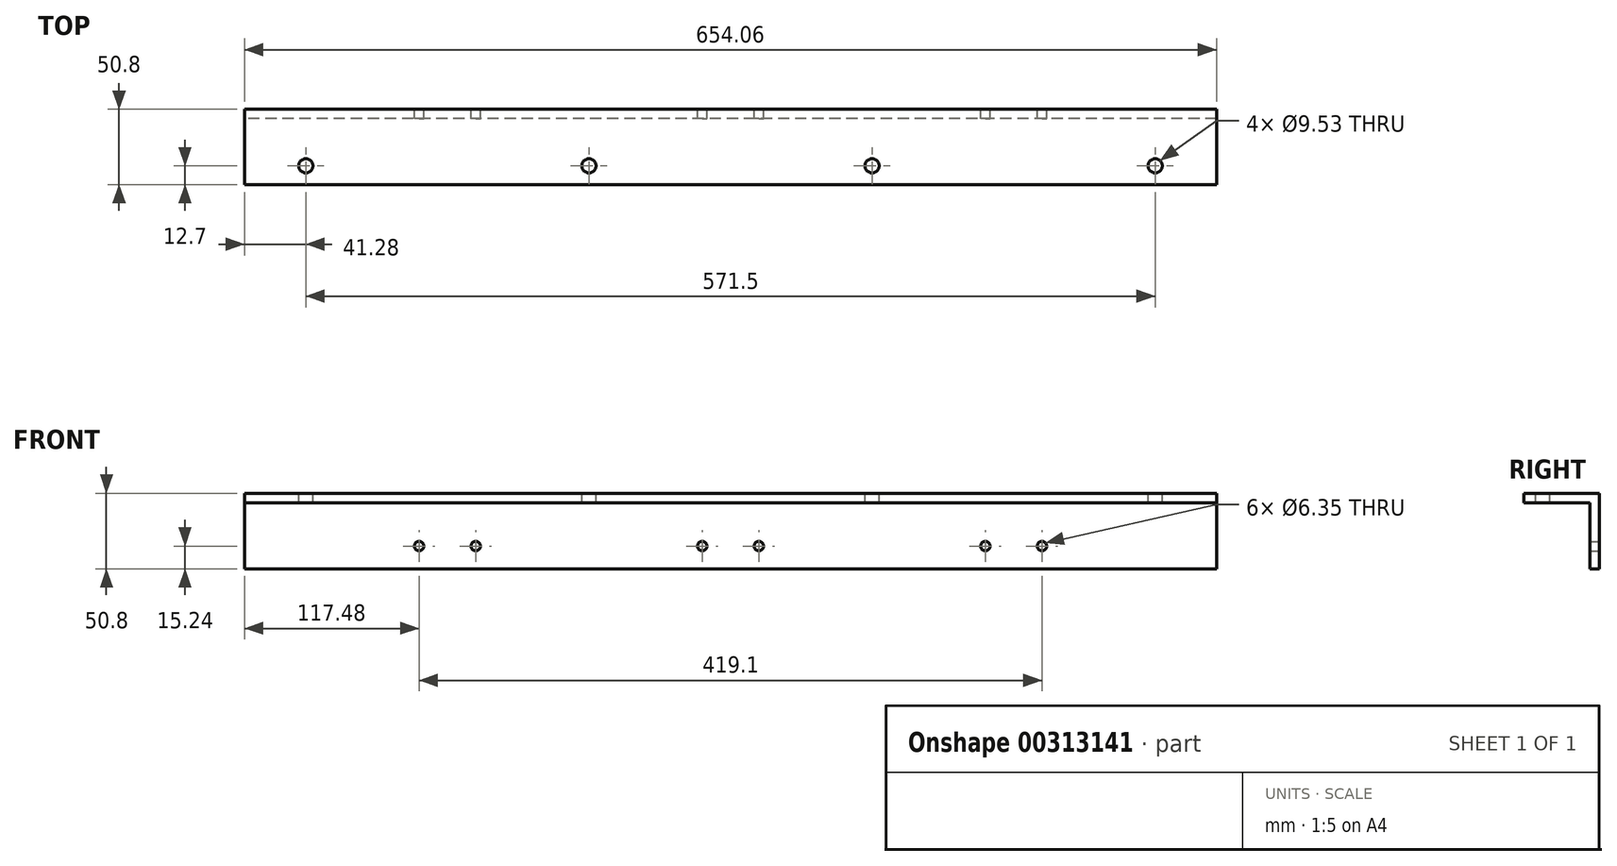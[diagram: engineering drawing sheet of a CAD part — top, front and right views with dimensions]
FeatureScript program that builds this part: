
annotation { "Feature Type Name" : "Feature", "Feature Type Description" : "" }
export const myFeature = defineFeature(function(context is Context, id is Id, definition is map)
    precondition{}
    {
        {
            var Q0;
            Q0=qCreatedBy(makeId("Right.planeOp"),FACE);
            var sketch = newSketch(context, id + "F0", { "sketchPlane" : qUnion([Q0])});
            skLineSegment(sketch, "E0", {"start": v(0, 0) * mm, "end": v(0, 44.45) * mm});
            skLineSegment(sketch, "E1", {"start": v(0, 44.45) * mm, "end": v(-44.45, 44.45) * mm});
            skLineSegment(sketch, "E2", {"start": v(-44.45, 44.45) * mm, "end": v(-44.45, 50.8) * mm});
            skLineSegment(sketch, "E3", {"start": v(-44.45, 50.8) * mm, "end": v(6.35, 50.8) * mm});
            skLineSegment(sketch, "E4", {"start": v(6.35, 50.8) * mm, "end": v(6.35, 0) * mm});
            skLineSegment(sketch, "E5", {"start": v(6.35, 0) * mm, "end": v(0, 0) * mm});
            skSolve(sketch);
        }
        {
            var Q0;
            Q0=qSketchRegion(id+"F0",true);
            extrude(context, id + "F1", {"entities" : qUnion([Q0]), "endBound" : BoundingType.SYMMETRIC, "depth" : 654.05 * mm});
        }
        {
            var Q0;
            Q0=makeQuery(id+"F1.opExtrude","SWEPT_FACE",FACE,{"disambiguationData":[OSD([sQuery(id+"F0.wireOp",EDGE,"E3")])]});
            var sketch = newSketch(context, id + "F2", { "sketchPlane" : qUnion([Q0])});
            skCircle(sketch, "E6", {"center": v(-285.75, -31.75) * mm, "radius": 4.76 * mm});
            skPoint(sketch, "E6.centerSnap0", {"position": v(-327.03, -19.05) * mm});
            skCircle(sketch, "E7.1.0.0", {"center": v(-95.25, -31.75) * mm, "radius": 4.76 * mm});
            skCircle(sketch, "E7.2.0.0", {"center": v(95.25, -31.75) * mm, "radius": 4.76 * mm});
            skCircle(sketch, "E7.3.0.0", {"center": v(285.75, -31.75) * mm, "radius": 4.76 * mm});
            skLineSegment(sketch, "E7.direction1", {"start": v(-285.75, -31.75) * mm, "end": v(-95.25, -31.75) * mm, "construction": true});
            skSolve(sketch);
        }
        {
            var Q0;
            Q0=qSketchRegion(id+"F2",true);
            extrude(context, id + "F3", {"entities" : qUnion([Q0]), "operationType" : NewBodyOperationType.REMOVE, "endBound" : BoundingType.THROUGH_ALL, "oppositeDirection" : true, "depth" : 25.4 * mm});
        }
        {
            var Q0;
            Q0=makeQuery(id+"F1.opExtrude","SWEPT_FACE",FACE,{"disambiguationData":[OSD([sQuery(id+"F0.wireOp",EDGE,"E4")])]});
            var sketch = newSketch(context, id + "F4", { "sketchPlane" : qUnion([Q0])});
            skPoint(sketch, "E8.centerSnap0", {"position": v(-327.03, 25.4) * mm});
            skCircle(sketch, "E9", {"center": v(209.55, 15.24) * mm, "radius": 3.18 * mm});
            skPoint(sketch, "E9.centerSnap0", {"position": v(327.03, 25.4) * mm});
            skCircle(sketch, "E10", {"center": v(171.45, 15.24) * mm, "radius": 3.18 * mm});
            skCircle(sketch, "E11.1.0.0", {"center": v(19.05, 15.24) * mm, "radius": 3.18 * mm});
            skCircle(sketch, "E11.1.0.1", {"center": v(-19.05, 15.24) * mm, "radius": 3.18 * mm});
            skCircle(sketch, "E11.2.0.0", {"center": v(-171.45, 15.24) * mm, "radius": 3.18 * mm});
            skCircle(sketch, "E11.2.0.1", {"center": v(-209.55, 15.24) * mm, "radius": 3.18 * mm});
            skLineSegment(sketch, "E11.direction1", {"start": v(171.45, 15.24) * mm, "end": v(-19.05, 15.24) * mm, "construction": true});
            skSolve(sketch);
        }
        {
            var Q0;
            Q0=qSketchRegion(id+"F4",true);
            extrude(context, id + "F5", {"entities" : qUnion([Q0]), "operationType" : NewBodyOperationType.REMOVE, "endBound" : BoundingType.THROUGH_ALL, "oppositeDirection" : true, "depth" : 25.4 * mm, "hasSecondDirection" : true, "secondDirectionBound" : SecondDirectionBoundingType.THROUGH_ALL, "secondDirectionOppositeDirection" : false, "secondDirectionDepth" : 25.4 * mm});
        }
    });
